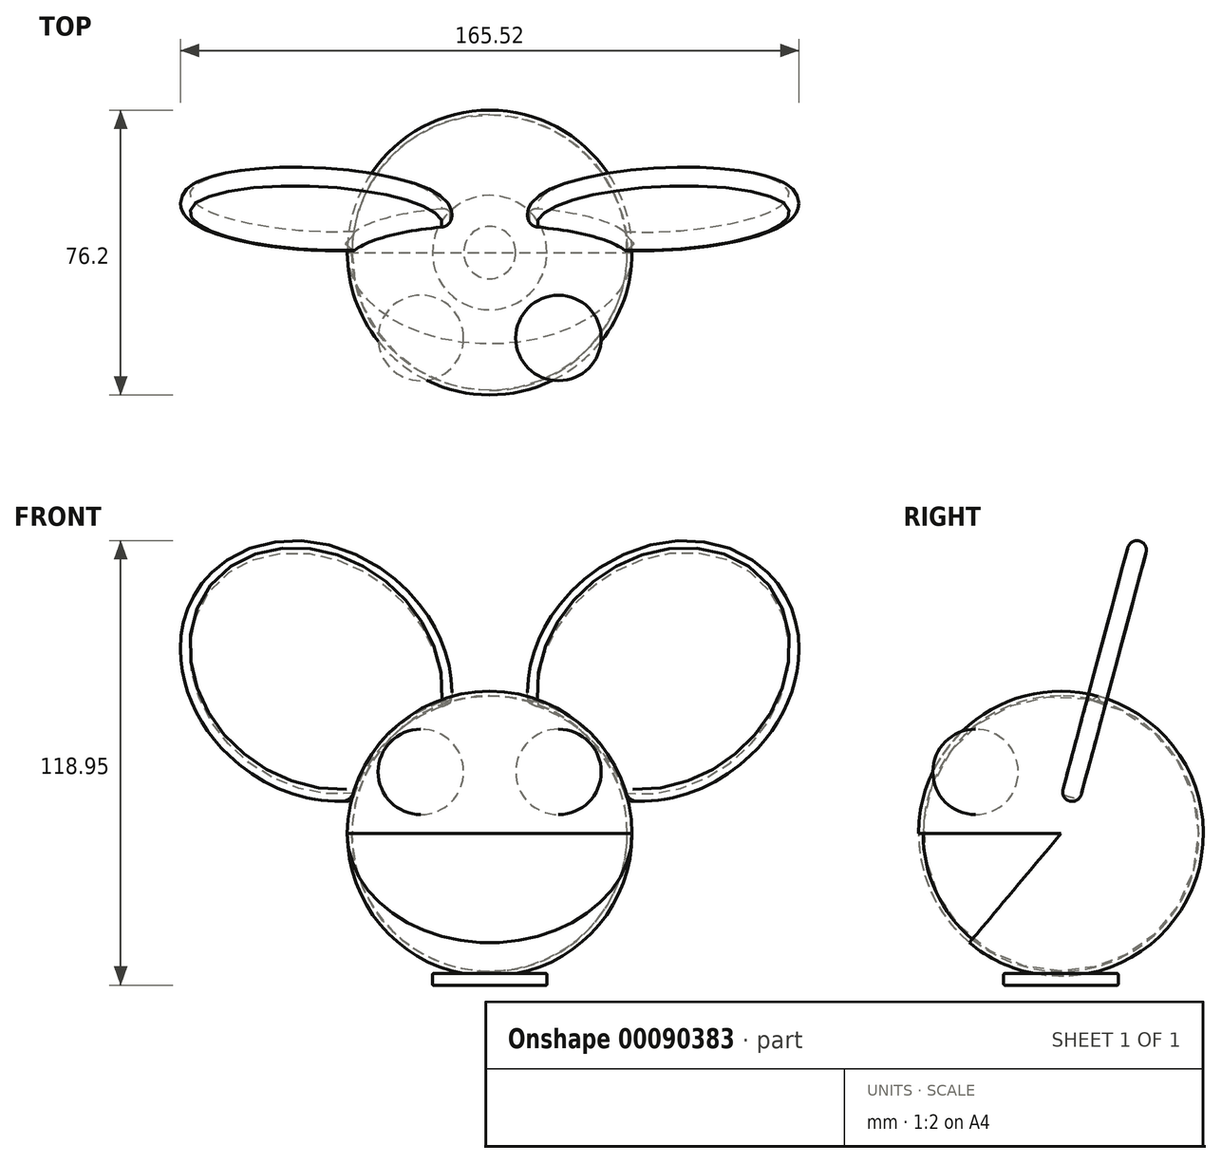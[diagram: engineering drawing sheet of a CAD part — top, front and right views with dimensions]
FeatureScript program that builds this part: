
annotation { "Feature Type Name" : "Feature", "Feature Type Description" : "" }
export const myFeature = defineFeature(function(context is Context, id is Id, definition is map)
    precondition{}
    {
        {
            var Q0;
            Q0=qCreatedBy(makeId("Front.planeOp"),FACE);
            var sketch = newSketch(context, id + "F0", { "sketchPlane" : qUnion([Q0])});
            skArc(sketch, "E0", {"start": v(38.1, 0) * mm, "mid": v(26.94, 26.94) * mm, "end": v(0, 38.1) * mm});
            skLineSegment(sketch, "E1", {"start": v(0, 0) * mm, "end": v(38.1, 0) * mm});
            skLineSegment(sketch, "E2", {"start": v(0, 0) * mm, "end": v(-38.1, 0) * mm});
            skArc(sketch, "E3", {"start": v(0, 38.1) * mm, "mid": v(-26.94, 26.94) * mm, "end": v(-38.1, 0) * mm});
            skPoint(sketch, "E4.orphan", {"position": v(0, -38.1) * mm});
            skSolve(sketch);
        }
        {
            var Q0;
            Q0=makeQuery(id+"F0.imprint","IMPRINT",FACE,{"disambiguationData":[TD([[makeQuery(id+"F0.imprint","IMPRINT",EDGE,{"derivedFrom":sQuery(id+"F0.wireOp",EDGE,"E0")}),1.0]])]});
            var Q1;
            Q1 = qSketchRegion(id + "F2", true);
            var Q2;
            Q2=sQuery(id+"F0.wireOp",EDGE,"E2");
            revolve(context, id + "F1", {"entities" : qUnion([Q0, Q1]), "axis" : qUnion([Q2]), "revolveType" : RevolveType.TWO_DIRECTIONS, "angle" : 220 * degree, "angleBack" : 270 * degree});
        }
        {
            var Q0;
            Q0=qCreatedBy(makeId("Top.planeOp"),FACE);
            var sketch = newSketch(context, id + "F2", { "sketchPlane" : qUnion([Q0])});
            skLineSegment(sketch, "E5", {"start": v(0, 0) * mm, "end": v(-36.83, 0) * mm});
            skLineSegment(sketch, "E6", {"start": v(0, 0) * mm, "end": v(36.83, 0) * mm});
            skArc(sketch, "E7.MirrorCS", {"start": v(36.83, 0) * mm, "mid": v(0, -36.9) * mm, "end": v(-36.83, 0) * mm});
            skSolve(sketch);
        }
        {
            var Q0;
            Q0=makeQuery(id+"F2.imprint","IMPRINT",FACE,{"disambiguationData":[TD([[makeQuery(id+"F2.imprint","IMPRINT",EDGE,{"derivedFrom":sQuery(id+"F2.wireOp",EDGE,"E5")}),1.0]])]});
            var Q1;
            Q1=sQuery(id+"F2.wireOp",EDGE,"E6");
            revolve(context, id + "F3", {"entities" : qUnion([Q0]), "axis" : qUnion([Q1]), "revolveType" : RevolveType.FULL});
        }
        {
            var Q0;
            Q0=qCreatedBy(makeId("Right.planeOp"),FACE);
            cPlane(context, id + "F4", {"entities" : qUnion([Q0]), "cplaneType" : CPlaneType.OFFSET, "offset" : 18.41 * mm, "width" : 152.4 * mm, "height" : 152.4 * mm});
        }
        {
            var Q0;
            Q0=qCreatedBy(id+"F4.planeOp",FACE);
            var sketch = newSketch(context, id + "F5", { "sketchPlane" : qUnion([Q0])});
            skLineSegment(sketch, "E8", {"start": v(0, 0) * mm, "end": v(0, 5.08) * mm});
            skLineSegment(sketch, "E9", {"start": v(0, 5.08) * mm, "end": v(-22.86, 5.08) * mm});
            skLineSegment(sketch, "E10", {"start": v(-22.86, 5.08) * mm, "end": v(-22.86, 16.5) * mm});
            skLineSegment(sketch, "E11", {"start": v(-22.86, 16.5) * mm, "end": v(-22.86, 27.94) * mm});
            skArc(sketch, "E12", {"start": v(-22.86, 27.94) * mm, "mid": v(-34.3, 16.5) * mm, "end": v(-22.86, 5.08) * mm});
            skSolve(sketch);
        }
        {
            var Q0;
            Q0 = qSketchRegion(id + "F5", true);
            var Q1;
            Q1=sQuery(id+"F5.wireOp",EDGE,"E11");
            revolve(context, id + "F6", {"entities" : qUnion([Q0]), "axis" : qUnion([Q1]), "revolveType" : RevolveType.FULL});
        }
        {
            var Q0;
            Q0=makeQuery(id+"F6.opRevolve","SWEPT_BODY",BODY,{"disambiguationData":[OSD([sQuery(id+"F5.wireOp",EDGE,"E10"),sQuery(id+"F5.wireOp",EDGE,"E11"),sQuery(id+"F5.wireOp",EDGE,"E12")])]});
            var Q1;
            Q1=qCreatedBy(makeId("Right.planeOp"),FACE);
            mirror(context, id + "F7", {"entities" : qUnion([Q0]), "mirrorPlane" : qUnion([Q1])});
        }
        {
            var Q0;
            Q0=qCreatedBy(makeId("Front.planeOp"),FACE);
            var sketch = newSketch(context, id + "F8", { "sketchPlane" : qUnion([Q0])});
            skLineSegment(sketch, "E13", {"start": v(0, 0) * mm, "end": v(-115.92, 0) * mm});
            skLineSegment(sketch, "E14", {"start": v(0, 0) * mm, "end": v(111.15, 0) * mm});
            skSolve(sketch);
        }
        {
            var Q0;
            Q0=sQuery(id+"F8.wireOp",EDGE,"E13");
            cPlane(context, id + "F9", {"entities" : qUnion([Q0]), "cplaneType" : CPlaneType.LINE_ANGLE, "offset" : 152.4 * mm, "angle" : 15 * degree, "width" : 152.4 * mm, "height" : 152.4 * mm});
        }
        {
            var Q0;
            Q0=qCreatedBy(id+"F9.planeOp",FACE);
            var sketch = newSketch(context, id + "F10", { "sketchPlane" : qUnion([Q0])});
            skEllipse(sketch, "E15", {"center": v(-46.44, 45.06) * mm, "majorRadius": 39.07 * mm, "minorRadius": 33.02 * mm, "majorAxis": v(0.72, -0.69)});
            skLineSegment(sketch, "E16", {"start": v(0, 39.56) * mm, "end": v(-8.9, 39.56) * mm});
            skLineSegment(sketch, "E17", {"start": v(0, 0) * mm, "end": v(-38.1, 0) * mm});
            skLineSegment(sketch, "E18", {"start": v(0, 0) * mm, "end": v(38.1, 0) * mm});
            skArc(sketch, "E19", {"start": v(38.1, 0) * mm, "mid": v(0, 37.58) * mm, "end": v(-38.1, 0) * mm});
            skLineSegment(sketch, "E20", {"start": v(-46.44, 45.06) * mm, "end": v(-74.73, 72) * mm});
            skLineSegment(sketch, "E21", {"start": v(-46.44, 45.06) * mm, "end": v(-26.9, 26.45) * mm});
            skSolve(sketch);
        }
        {
            var Q0;
            {var subQ0=sQuery(id+"F10.wireOp",EDGE,"E20");Q0=makeQuery(id+"F10.imprint","IMPRINT",FACE,{"disambiguationData":[TD([[makeQuery(id+"F10.imprint","IMPRINT",EDGE,{"derivedFrom":subQ0}),-1.0]])]});}
            var Q1;
            {var subQ0=sQuery(id+"F10.wireOp",EDGE,"E20");Q1=makeQuery(id+"F10.imprint","IMPRINT",FACE,{"disambiguationData":[TD([[makeQuery(id+"F10.imprint","IMPRINT",EDGE,{"derivedFrom":subQ0}),1.0]])]});}
            extrude(context, id + "F11", {"entities" : qUnion([Q0, Q1]), "endBound" : BoundingType.SYMMETRIC, "depth" : 5.08 * mm});
        }
        {
            var Q0;
            Q0=makeQuery(id+"F11.opExtrude","CAP_EDGE",EDGE,{"disambiguationData":[OSD([sQuery(id+"F10.wireOp",EDGE,"E15")])],"isStart":false});
            var Q1;
            Q1=makeQuery(id+"F11.opExtrude","SWEPT_FACE",FACE,{"disambiguationData":[OSD([sQuery(id+"F10.wireOp",EDGE,"E15")])]});
            fillet(context, id + "F12", {"entities" : qUnion([Q0, Q1]), "radius" : 2.54 * mm, "tangentPropagation" : true, "allowEdgeOverflow" : false});
        }
        {
            var Q0;
            Q0=makeQuery(id+"F11.opExtrude","SWEPT_BODY",BODY,{"disambiguationData":[OSD([sQuery(id+"F10.wireOp",EDGE,"E15"),sQuery(id+"F10.wireOp",EDGE,"E19")])]});
            var Q1;
            Q1=qCreatedBy(makeId("Right.planeOp"),FACE);
            mirror(context, id + "F13", {"operationType" : NewBodyOperationType.ADD, "entities" : qUnion([Q0]), "mirrorPlane" : qUnion([Q1])});
        }
        {
            var Q0;
            Q0=qCreatedBy(makeId("Front.planeOp"),FACE);
            var sketch = newSketch(context, id + "F14", { "sketchPlane" : qUnion([Q0])});
            skLineSegment(sketch, "E22.bottom", {"start": v(0, -37.45) * mm, "end": v(-15.31, -37.45) * mm});
            skLineSegment(sketch, "E22.top", {"start": v(0, -40.55) * mm, "end": v(-15.31, -40.55) * mm});
            skLineSegment(sketch, "E22.left", {"start": v(0, -37.45) * mm, "end": v(0, -40.55) * mm});
            skLineSegment(sketch, "E22.right", {"start": v(-15.31, -37.45) * mm, "end": v(-15.31, -40.55) * mm});
            skLineSegment(sketch, "E23.MirrorCS", {"start": v(0, -40.55) * mm, "end": v(15.31, -40.55) * mm});
            skLineSegment(sketch, "E24.MirrorCS", {"start": v(15.31, -37.45) * mm, "end": v(15.31, -40.55) * mm});
            skLineSegment(sketch, "E25.MirrorCS", {"start": v(0, -37.45) * mm, "end": v(15.31, -37.45) * mm});
            skSolve(sketch);
        }
        {
            var Q0;
            Q0=makeQuery(id+"F14.imprint","IMPRINT",FACE,{"disambiguationData":[TD([[makeQuery(id+"F14.imprint","IMPRINT",EDGE,{"derivedFrom":sQuery(id+"F14.wireOp",EDGE,"E22.left")}),1.0]])]});
            var Q1;
            Q1=sQuery(id+"F14.wireOp",EDGE,"E22.left");
            revolve(context, id + "F15", {"operationType" : NewBodyOperationType.ADD, "entities" : qUnion([Q0]), "axis" : qUnion([Q1]), "revolveType" : RevolveType.FULL});
        }
        {
            var Q0;
            Q0=makeQuery(id+"F15.opRevolve","SWEPT_EDGE",EDGE,{"disambiguationData":[OSD([sQuery(id+"F14.wireOp",EDGE,"E24.MirrorCS"),sQuery(id+"F14.wireOp",EDGE,"E25.MirrorCS")])]});
            var Q1;
            Q1=makeQuery(id+"F15.opRevolve","SWEPT_EDGE",EDGE,{"disambiguationData":[OSD([sQuery(id+"F14.wireOp",EDGE,"E23.MirrorCS"),sQuery(id+"F14.wireOp",EDGE,"E24.MirrorCS")])]});
            fillet(context, id + "F16", {"entities" : qUnion([Q0, Q1]), "radius" : 0.25 * mm, "tangentPropagation" : true, "allowEdgeOverflow" : false});
        }
    });
